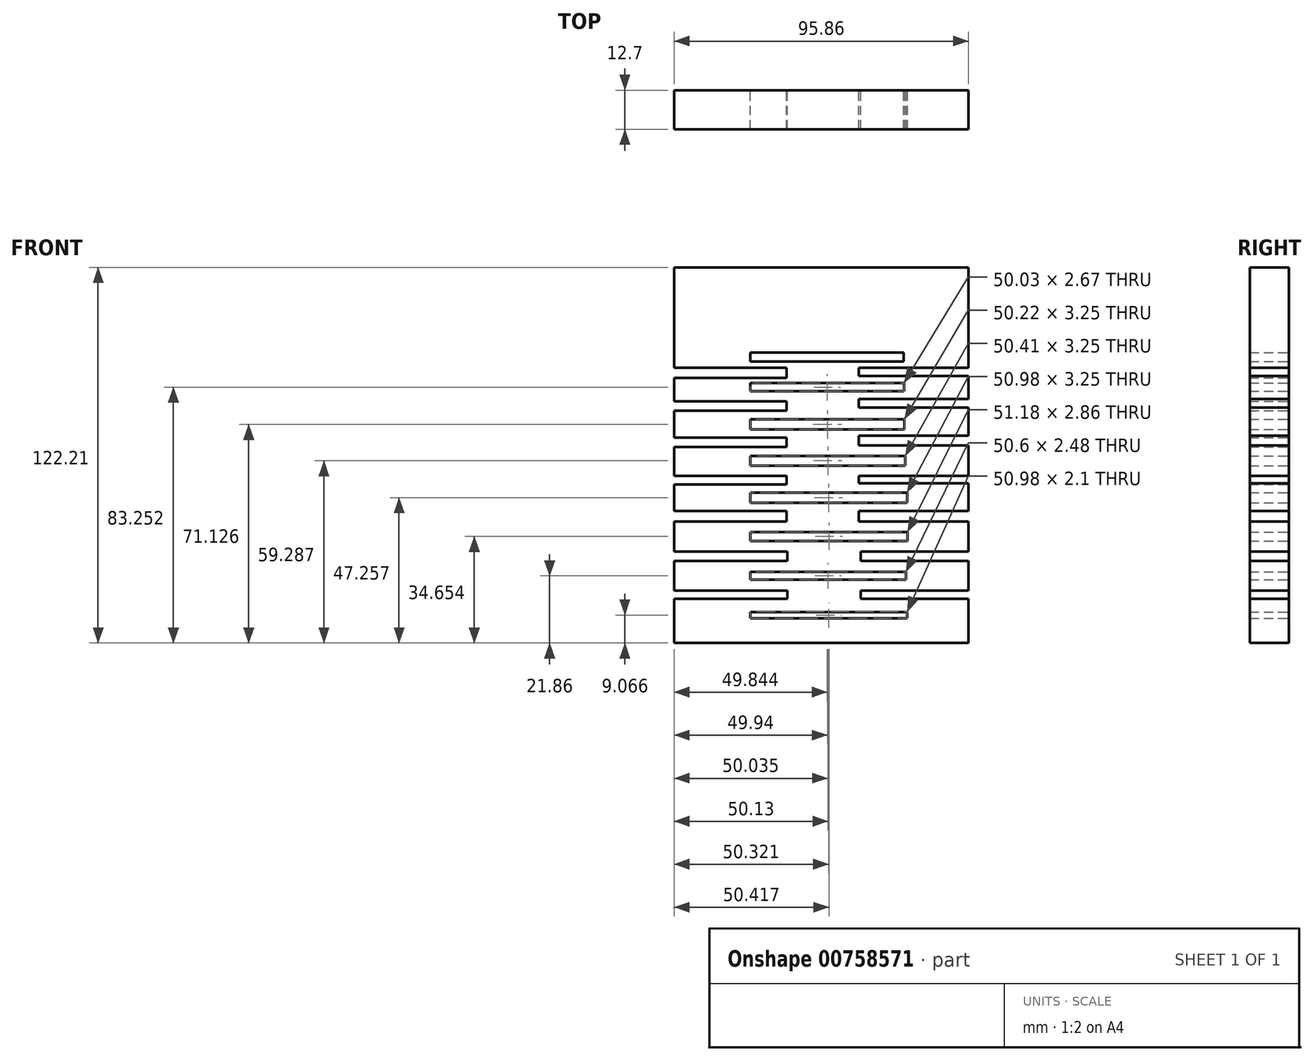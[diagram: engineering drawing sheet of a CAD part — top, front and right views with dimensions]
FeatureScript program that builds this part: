
annotation { "Feature Type Name" : "Feature", "Feature Type Description" : "" }
export const myFeature = defineFeature(function(context is Context, id is Id, definition is map)
    precondition{}
    {
        {
            var Q0;
            Q0=qCreatedBy(makeId("Front.planeOp"),FACE);
            var sketch = newSketch(context, id + "F0", { "sketchPlane" : qUnion([Q0])});
            skLineSegment(sketch, "E0.bottom", {"start": v(-48.03, -55.85) * mm, "end": v(47.83, -55.85) * mm});
            skLineSegment(sketch, "E0.top", {"start": v(-48.03, 66.36) * mm, "end": v(47.83, 66.36) * mm});
            skLineSegment(sketch, "E0.left", {"start": v(-48.03, -55.85) * mm, "end": v(-48.03, -41.53) * mm});
            skLineSegment(sketch, "E0.right", {"start": v(47.83, -55.85) * mm, "end": v(47.83, -41.53) * mm});
            skLineSegment(sketch, "E1.bottom", {"start": v(-23.2, -47.83) * mm, "end": v(27.78, -47.83) * mm});
            skLineSegment(sketch, "E1.top", {"start": v(-23.2, -45.73) * mm, "end": v(27.78, -45.73) * mm});
            skLineSegment(sketch, "E1.left", {"start": v(-23.2, -47.83) * mm, "end": v(-23.2, -45.73) * mm});
            skLineSegment(sketch, "E1.right", {"start": v(27.78, -47.83) * mm, "end": v(27.78, -45.73) * mm});
            skLineSegment(sketch, "E2.bottom", {"start": v(-48.03, -41.53) * mm, "end": v(-11.17, -41.53) * mm});
            skLineSegment(sketch, "E2.top", {"start": v(-48.03, -38.86) * mm, "end": v(-11.17, -38.86) * mm});
            skLineSegment(sketch, "E2.right", {"start": v(-11.17, -41.53) * mm, "end": v(-11.17, -38.86) * mm});
            skLineSegment(sketch, "E3.bottom", {"start": v(47.83, -38.86) * mm, "end": v(12.7, -38.86) * mm});
            skLineSegment(sketch, "E3.top", {"start": v(47.83, -41.53) * mm, "end": v(12.7, -41.53) * mm});
            skLineSegment(sketch, "E3.right", {"start": v(12.7, -38.86) * mm, "end": v(12.7, -41.53) * mm});
            skLineSegment(sketch, "E4.trimOffspring", {"start": v(47.83, -38.86) * mm, "end": v(47.83, -29.12) * mm});
            skLineSegment(sketch, "E5.trimOffspring", {"start": v(-48.03, -38.86) * mm, "end": v(-48.03, -29.12) * mm});
            skLineSegment(sketch, "E6.bottom", {"start": v(-23.2, -35.23) * mm, "end": v(27.4, -35.23) * mm});
            skLineSegment(sketch, "E6.top", {"start": v(-23.2, -32.75) * mm, "end": v(27.4, -32.75) * mm});
            skLineSegment(sketch, "E6.left", {"start": v(-23.2, -35.23) * mm, "end": v(-23.2, -32.75) * mm});
            skLineSegment(sketch, "E6.right", {"start": v(27.4, -35.23) * mm, "end": v(27.4, -32.75) * mm});
            skLineSegment(sketch, "E7.bottom", {"start": v(-11.17, -29.12) * mm, "end": v(-48.03, -29.12) * mm});
            skLineSegment(sketch, "E7.top", {"start": v(-11.17, -26.07) * mm, "end": v(-48.03, -26.07) * mm});
            skLineSegment(sketch, "E7.left", {"start": v(-11.17, -29.12) * mm, "end": v(-11.17, -26.07) * mm});
            skLineSegment(sketch, "E8.bottom", {"start": v(12.7, -29.12) * mm, "end": v(47.83, -29.12) * mm});
            skLineSegment(sketch, "E8.top", {"start": v(12.7, -26.07) * mm, "end": v(47.83, -26.07) * mm});
            skLineSegment(sketch, "E8.left", {"start": v(12.7, -29.12) * mm, "end": v(12.7, -26.07) * mm});
            skLineSegment(sketch, "E9.trimOffspring", {"start": v(47.83, -26.07) * mm, "end": v(47.83, -16.33) * mm});
            skLineSegment(sketch, "E10.trimOffspring", {"start": v(-48.03, -26.07) * mm, "end": v(-48.03, -16.33) * mm});
            skLineSegment(sketch, "E11.bottom", {"start": v(-23.2, -22.63) * mm, "end": v(27.97, -22.63) * mm});
            skLineSegment(sketch, "E11.top", {"start": v(-23.2, -19.76) * mm, "end": v(27.97, -19.76) * mm});
            skLineSegment(sketch, "E11.left", {"start": v(-23.2, -22.63) * mm, "end": v(-23.2, -19.76) * mm});
            skLineSegment(sketch, "E11.right", {"start": v(27.97, -22.63) * mm, "end": v(27.97, -19.76) * mm});
            skLineSegment(sketch, "E12.bottom", {"start": v(-11.36, -16.33) * mm, "end": v(-48.03, -16.33) * mm});
            skLineSegment(sketch, "E12.top", {"start": v(-11.36, -12.89) * mm, "end": v(-48.03, -12.89) * mm});
            skLineSegment(sketch, "E12.left", {"start": v(-11.36, -16.33) * mm, "end": v(-11.36, -12.89) * mm});
            skLineSegment(sketch, "E13.trimOffspring", {"start": v(-48.03, -12.89) * mm, "end": v(-48.03, -4.3) * mm});
            skLineSegment(sketch, "E14.bottom", {"start": v(12.13, -16.33) * mm, "end": v(47.83, -16.33) * mm});
            skLineSegment(sketch, "E14.top", {"start": v(12.13, -12.89) * mm, "end": v(47.83, -12.89) * mm});
            skLineSegment(sketch, "E14.left", {"start": v(12.13, -16.33) * mm, "end": v(12.13, -12.89) * mm});
            skLineSegment(sketch, "E15.trimOffspring", {"start": v(47.83, -12.89) * mm, "end": v(47.83, -3.91) * mm});
            skLineSegment(sketch, "E16.bottom", {"start": v(-23.2, -10.22) * mm, "end": v(27.78, -10.22) * mm});
            skLineSegment(sketch, "E16.top", {"start": v(-23.2, -6.97) * mm, "end": v(27.78, -6.97) * mm});
            skLineSegment(sketch, "E16.left", {"start": v(-23.2, -10.22) * mm, "end": v(-23.2, -6.97) * mm});
            skLineSegment(sketch, "E16.right", {"start": v(27.78, -10.22) * mm, "end": v(27.78, -6.97) * mm});
            skLineSegment(sketch, "E17.bottom", {"start": v(-11.36, -4.3) * mm, "end": v(-48.03, -4.3) * mm});
            skLineSegment(sketch, "E17.top", {"start": v(-11.36, -1.43) * mm, "end": v(-48.03, -1.43) * mm});
            skLineSegment(sketch, "E17.left", {"start": v(-11.36, -4.3) * mm, "end": v(-11.36, -1.43) * mm});
            skLineSegment(sketch, "E18.trimOffspring", {"start": v(-48.03, -1.43) * mm, "end": v(-48.03, 7.92) * mm});
            skLineSegment(sketch, "E19.bottom", {"start": v(12.13, -3.91) * mm, "end": v(47.83, -3.91) * mm});
            skLineSegment(sketch, "E19.top", {"start": v(12.13, -1.43) * mm, "end": v(47.83, -1.43) * mm});
            skLineSegment(sketch, "E19.left", {"start": v(12.13, -3.91) * mm, "end": v(12.13, -1.43) * mm});
            skLineSegment(sketch, "E20.trimOffspring", {"start": v(47.83, -1.43) * mm, "end": v(47.83, 8.5) * mm});
            skLineSegment(sketch, "E21.bottom", {"start": v(-23.2, 1.81) * mm, "end": v(27.21, 1.81) * mm});
            skLineSegment(sketch, "E21.top", {"start": v(-23.2, 5.06) * mm, "end": v(27.21, 5.06) * mm});
            skLineSegment(sketch, "E21.left", {"start": v(-23.2, 1.81) * mm, "end": v(-23.2, 5.06) * mm});
            skLineSegment(sketch, "E21.right", {"start": v(27.21, 1.81) * mm, "end": v(27.21, 5.06) * mm});
            skLineSegment(sketch, "E22.bottom", {"start": v(-11.36, 7.92) * mm, "end": v(-48.03, 7.92) * mm});
            skLineSegment(sketch, "E22.top", {"start": v(-11.36, 10.98) * mm, "end": v(-48.03, 10.98) * mm});
            skLineSegment(sketch, "E22.left", {"start": v(-11.36, 7.92) * mm, "end": v(-11.36, 10.98) * mm});
            skLineSegment(sketch, "E23.bottom", {"start": v(12.13, 8.5) * mm, "end": v(47.83, 8.5) * mm});
            skLineSegment(sketch, "E23.top", {"start": v(12.13, 11.55) * mm, "end": v(47.83, 11.55) * mm});
            skLineSegment(sketch, "E23.left", {"start": v(12.13, 8.5) * mm, "end": v(12.13, 11.55) * mm});
            skLineSegment(sketch, "E24.trimOffspring", {"start": v(-48.03, 10.98) * mm, "end": v(-48.03, 19.76) * mm});
            skLineSegment(sketch, "E25.trimOffspring", {"start": v(47.83, 11.55) * mm, "end": v(47.83, 20.72) * mm});
            skLineSegment(sketch, "E26.bottom", {"start": v(-23.2, 13.65) * mm, "end": v(27.02, 13.65) * mm});
            skLineSegment(sketch, "E26.top", {"start": v(-23.2, 16.9) * mm, "end": v(27.02, 16.9) * mm});
            skLineSegment(sketch, "E26.left", {"start": v(-23.2, 13.65) * mm, "end": v(-23.2, 16.9) * mm});
            skLineSegment(sketch, "E26.right", {"start": v(27.02, 13.65) * mm, "end": v(27.02, 16.9) * mm});
            skLineSegment(sketch, "E27.bottom", {"start": v(-11.36, 19.76) * mm, "end": v(-48.03, 19.76) * mm});
            skLineSegment(sketch, "E27.top", {"start": v(-11.36, 22.82) * mm, "end": v(-48.03, 22.82) * mm});
            skLineSegment(sketch, "E27.left", {"start": v(-11.36, 19.76) * mm, "end": v(-11.36, 22.82) * mm});
            skLineSegment(sketch, "E28.bottom", {"start": v(12.13, 20.72) * mm, "end": v(47.83, 20.72) * mm});
            skLineSegment(sketch, "E28.top", {"start": v(12.13, 23.58) * mm, "end": v(47.83, 23.58) * mm});
            skLineSegment(sketch, "E28.left", {"start": v(12.13, 20.72) * mm, "end": v(12.13, 23.58) * mm});
            skLineSegment(sketch, "E29.trimOffspring", {"start": v(47.83, 23.58) * mm, "end": v(47.83, 31.03) * mm});
            skLineSegment(sketch, "E30.trimOffspring", {"start": v(-48.03, 22.82) * mm, "end": v(-48.03, 30.46) * mm});
            skLineSegment(sketch, "E31.bottom", {"start": v(-23.2, 26.07) * mm, "end": v(26.83, 26.07) * mm});
            skLineSegment(sketch, "E31.top", {"start": v(-23.2, 28.74) * mm, "end": v(26.83, 28.74) * mm});
            skLineSegment(sketch, "E31.left", {"start": v(-23.2, 26.07) * mm, "end": v(-23.2, 28.74) * mm});
            skLineSegment(sketch, "E31.right", {"start": v(26.83, 26.07) * mm, "end": v(26.83, 28.74) * mm});
            skLineSegment(sketch, "E32.bottom", {"start": v(12.13, 31.03) * mm, "end": v(47.83, 31.03) * mm});
            skLineSegment(sketch, "E32.top", {"start": v(12.13, 33.7) * mm, "end": v(47.83, 33.7) * mm});
            skLineSegment(sketch, "E32.left", {"start": v(12.13, 31.03) * mm, "end": v(12.13, 33.7) * mm});
            skLineSegment(sketch, "E33.bottom", {"start": v(-11.36, 30.46) * mm, "end": v(-48.03, 30.46) * mm});
            skLineSegment(sketch, "E33.top", {"start": v(-11.36, 33.7) * mm, "end": v(-48.03, 33.7) * mm});
            skLineSegment(sketch, "E33.left", {"start": v(-11.36, 30.46) * mm, "end": v(-11.36, 33.7) * mm});
            skLineSegment(sketch, "E34.bottom", {"start": v(-23.2, 35.8) * mm, "end": v(26.64, 35.8) * mm});
            skLineSegment(sketch, "E34.top", {"start": v(-23.2, 38.67) * mm, "end": v(26.64, 38.67) * mm});
            skLineSegment(sketch, "E34.left", {"start": v(-23.2, 35.8) * mm, "end": v(-23.2, 38.67) * mm});
            skLineSegment(sketch, "E34.right", {"start": v(26.64, 35.8) * mm, "end": v(26.64, 38.67) * mm});
            skLineSegment(sketch, "E35.trimOffspring", {"start": v(-48.03, 33.7) * mm, "end": v(-48.03, 66.36) * mm});
            skLineSegment(sketch, "E36.trimOffspring", {"start": v(47.83, 33.7) * mm, "end": v(47.83, 66.36) * mm});
            skSolve(sketch);
        }
        {
            var Q0;
            Q0=qSketchRegion(id+"F0",true);
            extrude(context, id + "F1", {"entities" : qUnion([Q0]), "depth" : 12.7 * mm, "offsetDistance" : 25.4 * mm});
        }
    });
